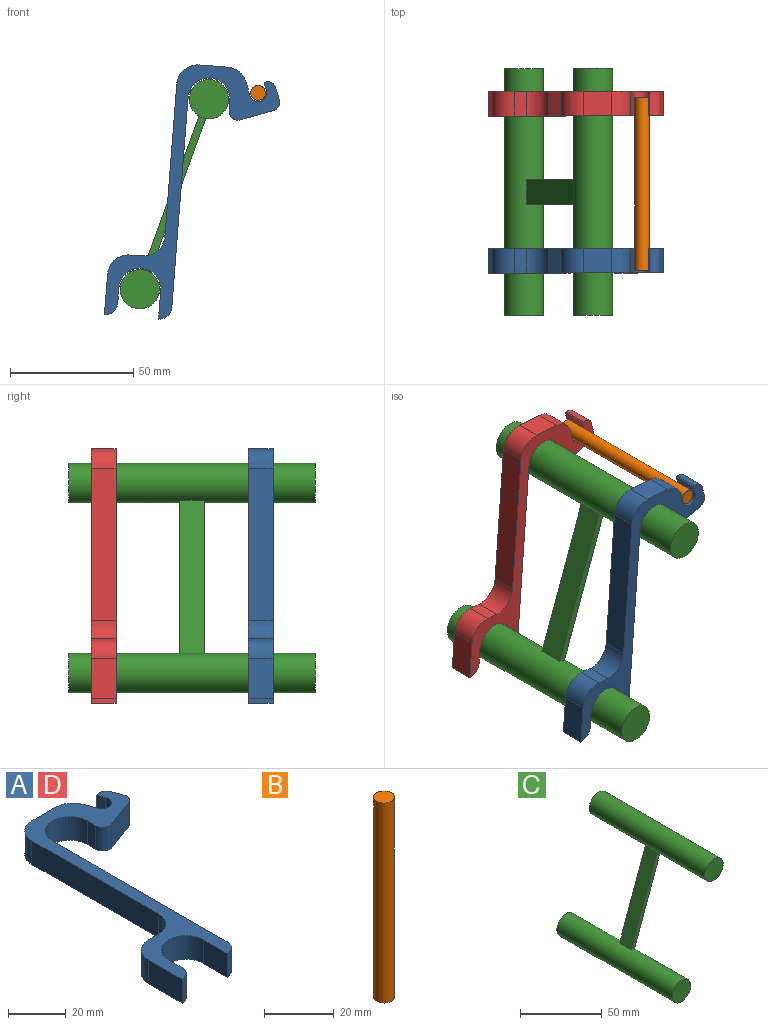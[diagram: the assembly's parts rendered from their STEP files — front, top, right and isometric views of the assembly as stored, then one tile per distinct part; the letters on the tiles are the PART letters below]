
ASSEMBLY  parts=4 mates=6
PART A: 27 faces, bbox 64.1x104x10 mm
  f0: plane 16.5x10mm, normal (-1,0,0), area 165mm2, adj f13,f14,f20,f25
  f1: plane 10x6.5mm, normal (1,0,0), area 65mm2, adj f13,f14,f15,f25
  f2: plane 11.5x10mm, normal (-1,0,0), area 115mm2, adj f13,f14,f15,f26
  f3: plane 85.49x10mm, normal (1,0,0), area 854.9mm2, adj f13,f14,f16,f26
  f4: plane 10x4.1mm, normal (-1,0,0), area 41mm2, adj f13,f14,f16,f21
  f5: plane 13.15x10mm, normal (0.34,-0.94,0), area 139.9mm2, adj f13,f14,f21,f22
  f6: plane 10x4.7mm, normal (0.94,0.34,0), area 50mm2, adj f13,f14,f22,f23
  f7: plane 10x0.47mm, normal (-0.34,0.94,0), area 5mm2, adj f8,f13,f14,f23
  f8: plane 10x3.29mm, normal (-0.94,-0.34,0), area 35mm2, adj f7,f13,f14,f24
  f9: plane 10x5.09mm, normal (0.94,0.34,0), area 54.2mm2, adj f13,f14,f17,f24
  f10: plane 11.55x10mm, normal (0,1,0), area 115.5mm2, adj f13,f14,f17,f18
  f11: plane 61.99x10mm, normal (-1,0,0), area 619.9mm2, adj f13,f14,f18,f19
  f12: plane 10x5mm, normal (0,1,0), area 50mm2, adj f13,f14,f19,f20
  f13: plane 103.99x64.15mm, normal (0,0,1), area 1080.9mm2, adj f0,f1,f2,f3,f4,f5,f6,f7
  f14: plane 103.99x64.15mm, normal (0,0,-1), area 1080.9mm2, adj f0,f1,f2,f3,f4,f5,f6,f7
  f15: cylinder r=8.5mm len=17mm, axis (0,0,1), area 267mm2, adj f1,f2,f13,f14
  f16: cylinder r=8.5mm len=17mm, axis (0,0,1), area 267mm2, adj f3,f4,f13,f14
  f17: cylinder r=8.5mm len=10mm, axis (0,0,-1), area 103.8mm2, adj f9,f10,f13,f14
  f18: cylinder r=8.5mm len=10mm, axis (0,0,-1), area 133.5mm2, adj f10,f11,f13,f14
  f19: cylinder r=8.5mm len=10mm, axis (0,0,1), area 133.5mm2, adj f11,f12,f13,f14
  f20: cylinder r=8.5mm len=10mm, axis (0,0,-1), area 133.5mm2, adj f0,f12,f13,f14
  f21: cylinder r=3.5mm len=10mm, axis (0,0,-1), area 67.2mm2, adj f4,f5,f13,f14
  f22: cylinder r=3.5mm len=10mm, axis (0,0,-1), area 55mm2, adj f5,f6,f13,f14
  f23: cylinder r=3.5mm len=10mm, axis (0,0,-1), area 55mm2, adj f6,f7,f13,f14
  f24: cylinder r=3.5mm len=10mm, axis (0,0,1), area 110mm2, adj f8,f9,f13,f14
  f25: cylinder r=5mm len=10mm, axis (0,0,-1), area 78.5mm2, adj f0,f1,f13,f14
  f26: cylinder r=5mm len=10mm, axis (0,0,-1), area 78.5mm2, adj f2,f3,f13,f14
PART B: 3 faces, bbox 6x6x70 mm
  f0: cylinder r=3mm len=70mm, axis (0,0,-1), area 1319.5mm2, adj f1,f2
  f1: plane 6x6mm, normal (0,0,1), area 28.3mm2, adj f0
  f2: plane 6x6mm, normal (0,0,-1), area 28.3mm2, adj f0
PART C: 10 faces, bbox 44x100x93.1 mm
  f0: cylinder r=8mm len=100mm, axis (0,1,0), area 4996.4mm2, adj f1,f2,f6,f7,f8,f9
  f1: plane 16x16mm, normal (0,-1,0), area 201.1mm2, adj f0
  f2: plane 16x16mm, normal (0,1,0), area 201.1mm2, adj f0
  f3: cylinder r=8mm len=100mm, axis (0,1,0), area 4996.4mm2, adj f4,f5,f6,f7,f8,f9
  f4: plane 16x16mm, normal (0,-1,0), area 201.1mm2, adj f3
  f5: plane 16x16mm, normal (0,1,0), area 201.1mm2, adj f3
  f6: plane 62.29x22.67mm, normal (0.94,0,-0.34), area 662.8mm2, adj f0,f3,f8,f9
  f7: plane 62.29x22.67mm, normal (-0.94,0,0.34), area 662.8mm2, adj f0,f3,f8,f9
  f8: plane 63.31x25.49mm, normal (0,-1,0), area 198.3mm2, adj f0,f3,f6,f7
  f9: plane 63.31x25.49mm, normal (0,1,0), area 198.3mm2, adj f0,f3,f6,f7
PART D: same geometry as A
PLACE A rot(axis=(1,0.04,-0.04),90.1deg) t=(-56.6,-12.46,-51.16)mm
PLACE B rot(axis=(-0.61,-0.56,-0.56),117.5deg) t=(5.72,-21.35,38.8)mm
PLACE C t=(-42.26,10.45,-40.74)mm fixed
PLACE D rot(axis=(1,0.04,-0.04),90.1deg) t=(-56.6,51.24,-51.16)mm
MATE slider A.f24 <-> B.f0  axis (0,-1,0) through (5.72,-22.46,38.8)mm
MATE cylindrical A.f15 <-> C.f0  axis (0,-1,0) through (-42.26,-22.46,-40.74)mm
MATE cylindrical A.f16 <-> C.f3  axis (0,-1,0) through (-14.21,-22.46,36.32)mm
MATE cylindrical A.f15 <-> C.f0  axis (0,-1,0) through (-42.26,-17.46,-40.74)mm
MATE cylindrical D.f16 <-> C.f3  axis (0,-1,0) through (-14.21,51.24,36.32)mm
MATE cylindrical C.f0 <-> D.f15  axis (0,1,0) through (-42.26,60.45,-40.74)mm
